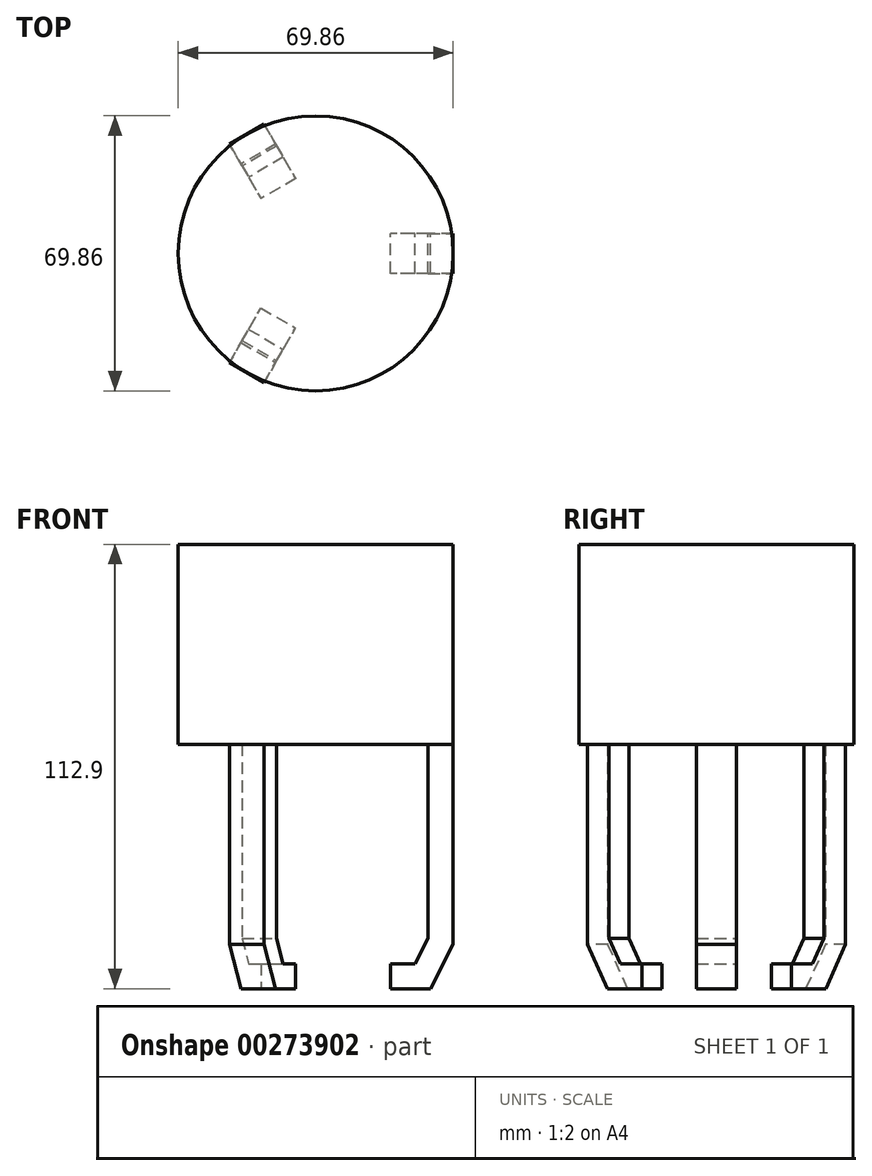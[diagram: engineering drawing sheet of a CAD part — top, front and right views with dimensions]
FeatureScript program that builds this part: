
annotation { "Feature Type Name" : "Feature", "Feature Type Description" : "" }
export const myFeature = defineFeature(function(context is Context, id is Id, definition is map)
    precondition{}
    {
        {
            var Q0;
            Q0=qCreatedBy(makeId("Top.planeOp"),FACE);
            var sketch = newSketch(context, id + "F0", { "sketchPlane" : qUnion([Q0])});
            skCircle(sketch, "E0", {"center": v(0, 0) * mm, "radius": 34.93 * mm});
            skSolve(sketch);
        }
        {
            var Q0;
            Q0 = qSketchRegion(id + "F0", true);
            extrude(context, id + "F1", {"entities" : qUnion([Q0]), "depth" : 50.8 * mm});
        }
        {
            var Q0;
            Q0=qCreatedBy(makeId("Front.planeOp"),FACE);
            var sketch = newSketch(context, id + "F2", { "sketchPlane" : qUnion([Q0])});
            skLineSegment(sketch, "E1", {"start": v(34.93, 0) * mm, "end": v(34.93, -50.8) * mm});
            skLineSegment(sketch, "E2", {"start": v(34.93, -50.8) * mm, "end": v(29.12, -62.1) * mm});
            skLineSegment(sketch, "E3", {"start": v(29.12, -62.1) * mm, "end": v(18.96, -62.1) * mm});
            skLineSegment(sketch, "E4.0", {"start": v(25.24, -55.75) * mm, "end": v(18.96, -55.75) * mm});
            skLineSegment(sketch, "E4.1", {"start": v(28.58, -49.26) * mm, "end": v(25.24, -55.75) * mm});
            skLineSegment(sketch, "E4.2", {"start": v(28.58, 0) * mm, "end": v(28.58, -49.26) * mm});
            skLineSegment(sketch, "E5", {"start": v(18.96, -55.75) * mm, "end": v(18.96, -62.1) * mm});
            skLineSegment(sketch, "E6", {"start": v(28.58, 0) * mm, "end": v(34.93, 0) * mm});
            skSolve(sketch);
        }
        {
            var Q0;
            Q0 = qSketchRegion(id + "F2", true);
            extrude(context, id + "F3", {"entities" : qUnion([Q0]), "endBound" : BoundingType.SYMMETRIC, "depth" : 10.16 * mm});
        }
        {
            var Q0;
            Q0=makeQuery(id+"F3.opExtrude","SWEPT_BODY",BODY,{"disambiguationData":[OSD([sQuery(id+"F2.wireOp",EDGE,"E1"),sQuery(id+"F2.wireOp",EDGE,"E2"),sQuery(id+"F2.wireOp",EDGE,"E3"),sQuery(id+"F2.wireOp",EDGE,"E4.0"),sQuery(id+"F2.wireOp",EDGE,"E4.1"),sQuery(id+"F2.wireOp",EDGE,"E4.2"),sQuery(id+"F2.wireOp",EDGE,"E5"),sQuery(id+"F2.wireOp",EDGE,"E6")])]});
            var Q1;
            Q1=makeQuery(id+"F1.opExtrude","CAP_EDGE",EDGE,{"disambiguationData":[OSD([sQuery(id+"F0.wireOp",EDGE,"E0")])],"isStart":false});
            transform(context, id + "F4", {"entities" : qUnion([Q0]), "transformType" : TransformType.ROTATION, "transformAxis" : qUnion([Q1]), "angle" : 120 * degree, "makeCopy" : true});
        }
        {
            var Q0;
            Q0=makeQuery(id+"F3.opExtrude","SWEPT_BODY",BODY,{"disambiguationData":[OSD([sQuery(id+"F2.wireOp",EDGE,"E1"),sQuery(id+"F2.wireOp",EDGE,"E2"),sQuery(id+"F2.wireOp",EDGE,"E3"),sQuery(id+"F2.wireOp",EDGE,"E4.0"),sQuery(id+"F2.wireOp",EDGE,"E4.1"),sQuery(id+"F2.wireOp",EDGE,"E4.2"),sQuery(id+"F2.wireOp",EDGE,"E5"),sQuery(id+"F2.wireOp",EDGE,"E6")])]});
            var Q1;
            Q1=makeQuery(id+"F1.opExtrude","CAP_EDGE",EDGE,{"disambiguationData":[OSD([sQuery(id+"F0.wireOp",EDGE,"E0")])],"isStart":false});
            transform(context, id + "F5", {"entities" : qUnion([Q0]), "transformType" : TransformType.ROTATION, "transformAxis" : qUnion([Q1]), "angle" : 240 * degree, "makeCopy" : true});
        }
    });
